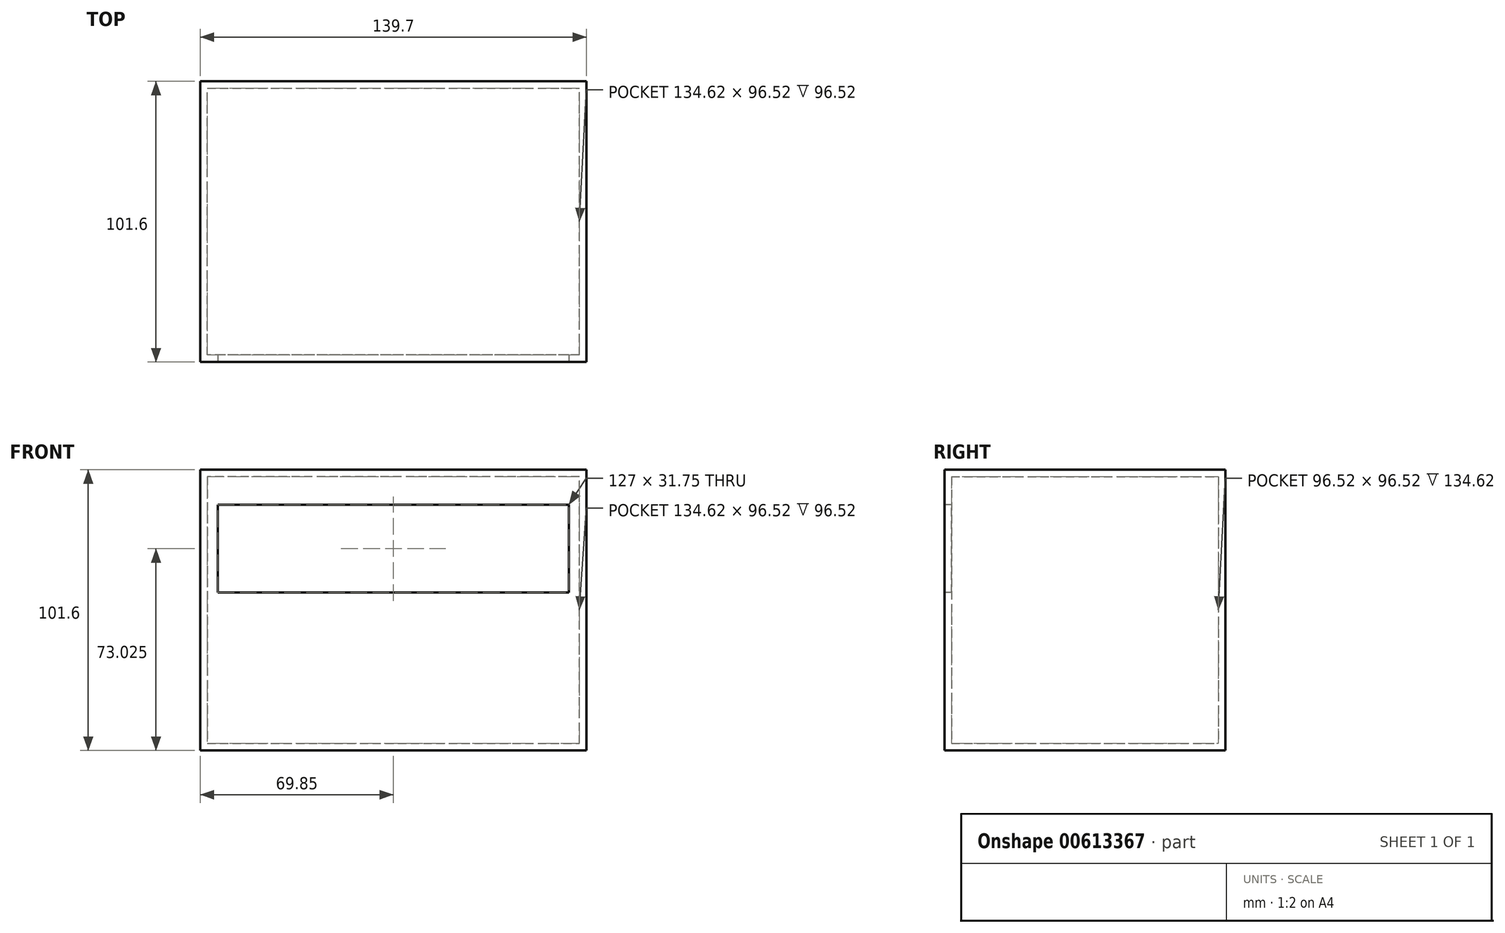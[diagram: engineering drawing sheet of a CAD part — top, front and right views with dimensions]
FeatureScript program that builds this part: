
annotation { "Feature Type Name" : "Feature", "Feature Type Description" : "" }
export const myFeature = defineFeature(function(context is Context, id is Id, definition is map)
    precondition{}
    {
        {
            var Q0;
            Q0=qCreatedBy(makeId("Front.planeOp"),FACE);
            var sketch = newSketch(context, id + "F0", { "sketchPlane" : qUnion([Q0])});
            skLineSegment(sketch, "E0", {"start": v(0, 0) * mm, "end": v(139.7, 0) * mm});
            skLineSegment(sketch, "E1", {"start": v(139.7, 0) * mm, "end": v(139.7, 101.6) * mm});
            skLineSegment(sketch, "E2", {"start": v(139.7, 101.6) * mm, "end": v(0, 101.6) * mm});
            skLineSegment(sketch, "E3", {"start": v(0, 101.6) * mm, "end": v(0, 0) * mm});
            skSolve(sketch);
        }
        {
            var Q0;
            Q0=makeQuery(id+"F0.imprint","IMPRINT",FACE,{"disambiguationData":[TD([[makeQuery(id+"F0.imprint","IMPRINT",EDGE,{"derivedFrom":sQuery(id+"F0.wireOp",EDGE,"E0")}),1.0]])]});
            extrude(context, id + "F1", {"entities" : qUnion([Q0]), "depth" : 101.6 * mm, "offsetDistance" : 25.4 * mm});
        }
        {
            var Q0;
            Q0=makeQuery(id+"F1.opExtrude","CAP_FACE",FACE,{"disambiguationData":[OSD([sQuery(id+"F0.wireOp",EDGE,"E0"),sQuery(id+"F0.wireOp",EDGE,"E1"),sQuery(id+"F0.wireOp",EDGE,"E2"),sQuery(id+"F0.wireOp",EDGE,"E3")])],"isStart":false});
            var Q1;
            Q1=makeQuery(id+"F1.opExtrude","SWEPT_BODY",BODY,{"disambiguationData":[OSD([sQuery(id+"F0.wireOp",EDGE,"E0"),sQuery(id+"F0.wireOp",EDGE,"E1"),sQuery(id+"F0.wireOp",EDGE,"E2"),sQuery(id+"F0.wireOp",EDGE,"E3")])]});
            shell(context, id + "F2", {"isHollow" : true, "entities" : qUnion([Q0]), "parts" : qUnion([Q1]), "thickness" : 2.54 * mm});
        }
        {
            var Q0;
            Q0=makeQuery(id+"F1.opExtrude","CAP_FACE",FACE,{"disambiguationData":[OSD([sQuery(id+"F0.wireOp",EDGE,"E0"),sQuery(id+"F0.wireOp",EDGE,"E1"),sQuery(id+"F0.wireOp",EDGE,"E2"),sQuery(id+"F0.wireOp",EDGE,"E3")])],"isStart":false});
            var sketch = newSketch(context, id + "F3", { "sketchPlane" : qUnion([Q0])});
            skLineSegment(sketch, "E4", {"start": v(6.35, 57.15) * mm, "end": v(6.35, 88.9) * mm});
            skLineSegment(sketch, "E5", {"start": v(6.35, 88.9) * mm, "end": v(133.35, 88.9) * mm});
            skLineSegment(sketch, "E6", {"start": v(133.35, 88.9) * mm, "end": v(133.35, 57.15) * mm});
            skLineSegment(sketch, "E7", {"start": v(133.35, 57.15) * mm, "end": v(6.35, 57.15) * mm});
            skSolve(sketch);
        }
        {
            var Q0;
            Q0=makeQuery(id+"F3.imprint","IMPRINT",FACE,{"disambiguationData":[TD([[makeQuery(id+"F3.imprint","IMPRINT",EDGE,{"derivedFrom":sQuery(id+"F3.wireOp",EDGE,"E4")}),-1.0]])]});
            extrude(context, id + "F4", {"entities" : qUnion([Q0]), "operationType" : NewBodyOperationType.REMOVE, "oppositeDirection" : true, "depth" : 25.4 * mm, "offsetDistance" : 25.4 * mm});
        }
    });
